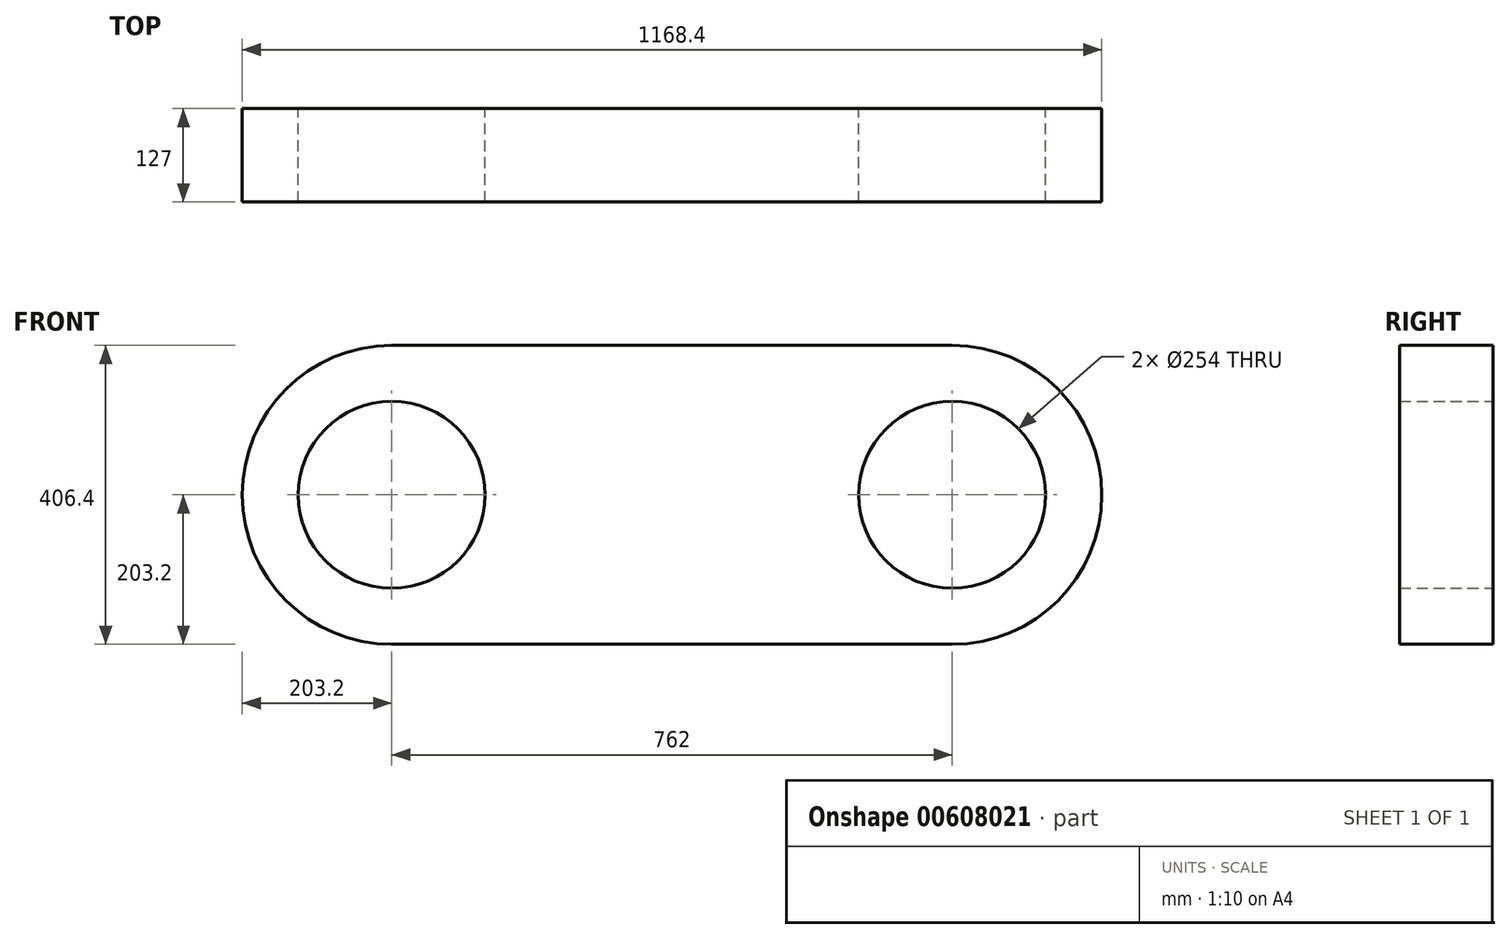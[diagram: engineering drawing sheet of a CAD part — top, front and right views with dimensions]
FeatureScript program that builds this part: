
annotation { "Feature Type Name" : "Feature", "Feature Type Description" : "" }
export const myFeature = defineFeature(function(context is Context, id is Id, definition is map)
    precondition{}
    {
        {
            var Q0;
            Q0=qCreatedBy(makeId("Front.planeOp"),FACE);
            var sketch = newSketch(context, id + "F0", { "sketchPlane" : qUnion([Q0])});
            skLineSegment(sketch, "E0.bottom", {"start": v(-381, 203.2) * mm, "end": v(381, 203.2) * mm});
            skLineSegment(sketch, "E0.top", {"start": v(-381, -203.2) * mm, "end": v(381, -203.2) * mm});
            skArc(sketch, "E1", {"start": v(-381, 203.2) * mm, "mid": v(-584.2, 0) * mm, "end": v(-381, -203.2) * mm});
            skArc(sketch, "E2", {"start": v(381, -203.2) * mm, "mid": v(584.2, 0) * mm, "end": v(381, 203.2) * mm});
            skCircle(sketch, "E3", {"center": v(381, 0) * mm, "radius": 127 * mm});
            skCircle(sketch, "E4", {"center": v(-381, 0) * mm, "radius": 127 * mm});
            skSolve(sketch);
        }
        {
            var Q0;
            Q0 = qSketchRegion(id + "F0", true);
            extrude(context, id + "F1", {"entities" : qUnion([Q0]), "endBound" : BoundingType.SYMMETRIC, "depth" : 127 * mm, "offsetDistance" : 25.4 * mm});
        }
    });
